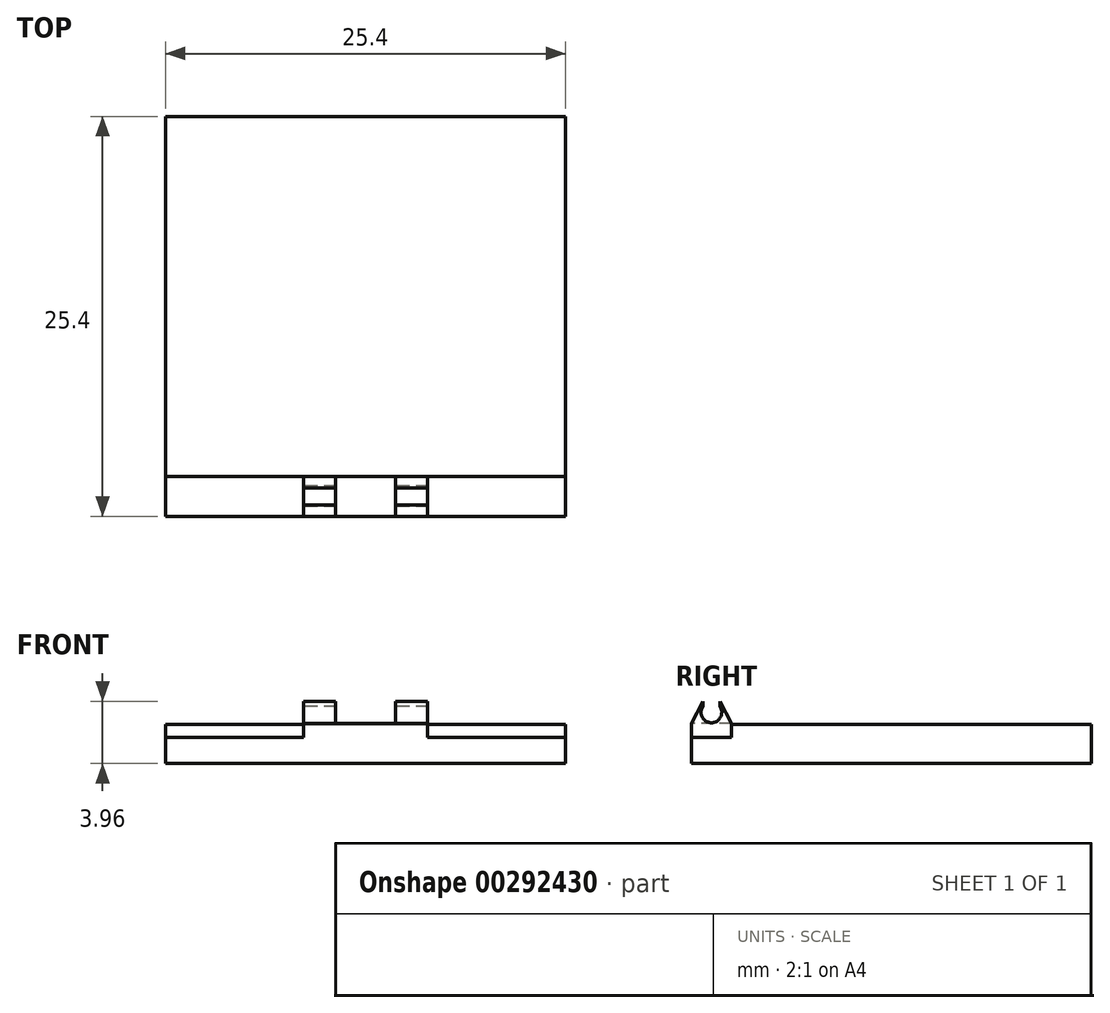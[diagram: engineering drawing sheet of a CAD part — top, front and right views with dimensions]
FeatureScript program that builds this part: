
annotation { "Feature Type Name" : "Feature", "Feature Type Description" : "" }
export const myFeature = defineFeature(function(context is Context, id is Id, definition is map)
    precondition{}
    {
        {
            var Q0;
            Q0=qCreatedBy(makeId("Top.planeOp"),FACE);
            var sketch = newSketch(context, id + "F0", { "sketchPlane" : qUnion([Q0])});
            skLineSegment(sketch, "E0.bottom", {"start": v(-9.72, 18.37) * mm, "end": v(15.68, 18.37) * mm});
            skLineSegment(sketch, "E0.top", {"start": v(-9.72, -7.03) * mm, "end": v(15.68, -7.03) * mm});
            skLineSegment(sketch, "E0.left", {"start": v(-9.72, 18.37) * mm, "end": v(-9.72, -7.03) * mm});
            skLineSegment(sketch, "E0.right", {"start": v(15.68, 18.37) * mm, "end": v(15.68, -7.03) * mm});
            skSolve(sketch);
        }
        {
            var Q0;
            Q0=qSketchRegion(id+"F0",true);
            extrude(context, id + "F1", {"entities" : qUnion([Q0]), "oppositeDirection" : true, "depth" : 2.54 * mm});
        }
        {
            var Q0;
            Q0=makeQuery(id+"F1.opExtrude","CAP_FACE",FACE,{"disambiguationData":[OSD([sQuery(id+"F0.wireOp",EDGE,"E0.bottom"),sQuery(id+"F0.wireOp",EDGE,"E0.top"),sQuery(id+"F0.wireOp",EDGE,"E0.left"),sQuery(id+"F0.wireOp",EDGE,"E0.right")])],"isStart":true});
            var sketch = newSketch(context, id + "F2", { "sketchPlane" : qUnion([Q0])});
            skLineSegment(sketch, "E1.bottom", {"start": v(-2.1, -7.03) * mm, "end": v(8.06, -7.03) * mm});
            skLineSegment(sketch, "E1.top", {"start": v(-2.1, -4.5) * mm, "end": v(8.06, -4.5) * mm});
            skLineSegment(sketch, "E1.left", {"start": v(-2.1, -7.03) * mm, "end": v(-2.1, -4.5) * mm});
            skLineSegment(sketch, "E1.right", {"start": v(8.06, -7.03) * mm, "end": v(8.06, -4.5) * mm});
            skSolve(sketch);
        }
        {
            var Q0;
            Q0=qSketchRegion(id+"F2",true);
            extrude(context, id + "F3", {"entities" : qUnion([Q0]), "operationType" : NewBodyOperationType.ADD, "depth" : 1.42 * mm});
        }
        {
            var Q0;
            Q0=makeQuery(id+"F3.opExtrude","SWEPT_FACE",FACE,{"disambiguationData":[OSD([sQuery(id+"F2.wireOp",EDGE,"E1.left")])]});
            var sketch = newSketch(context, id + "F4", { "sketchPlane" : qUnion([Q0])});
            skCircle(sketch, "E2", {"center": v(5.76, 0.71) * mm, "radius": 0.66 * mm});
            skPoint(sketch, "E3.endSnap0", {"position": v(5.76, 1.42) * mm});
            skLineSegment(sketch, "E4.bottom", {"start": v(5.22, 1.42) * mm, "end": v(6.32, 1.42) * mm});
            skLineSegment(sketch, "E4.left", {"start": v(5.22, 1.42) * mm, "end": v(5.22, 1.08) * mm});
            skLineSegment(sketch, "E4.right", {"start": v(6.32, 1.42) * mm, "end": v(6.32, 1.08) * mm});
            skLineSegment(sketch, "E5", {"start": v(5.22, 1.42) * mm, "end": v(4.5, 0) * mm});
            skLineSegment(sketch, "E6", {"start": v(6.32, 1.42) * mm, "end": v(7.03, 0) * mm});
            skSolve(sketch);
        }
        {
            var Q0;
            Q0=makeQuery(id+"F3.boolean.opBoolean","MERGE",FACE,{"derivedFrom":[makeQuery(id+"F1.opExtrude","SWEPT_FACE",FACE,{"disambiguationData":[OSD([sQuery(id+"F0.wireOp",EDGE,"E0.top")])]}),makeQuery(id+"F3.opExtrude","SWEPT_FACE",FACE,{"disambiguationData":[OSD([sQuery(id+"F2.wireOp",EDGE,"E1.bottom")])]})]});
            var sketch = newSketch(context, id + "F5", { "sketchPlane" : qUnion([Q0])});
            skLineSegment(sketch, "E7.bottom", {"start": v(-0.95, 1.42) * mm, "end": v(1.08, 1.42) * mm});
            skLineSegment(sketch, "E7.top", {"start": v(-0.95, 0) * mm, "end": v(1.08, 0) * mm});
            skLineSegment(sketch, "E7.left", {"start": v(-0.95, 1.42) * mm, "end": v(-0.95, 0) * mm});
            skLineSegment(sketch, "E7.right", {"start": v(1.08, 1.42) * mm, "end": v(1.08, 0) * mm});
            skLineSegment(sketch, "E8.bottom", {"start": v(4.89, 1.42) * mm, "end": v(6.92, 1.42) * mm});
            skLineSegment(sketch, "E8.top", {"start": v(4.89, 0) * mm, "end": v(6.92, 0) * mm});
            skLineSegment(sketch, "E8.left", {"start": v(4.89, 1.42) * mm, "end": v(4.89, 0) * mm});
            skLineSegment(sketch, "E8.right", {"start": v(6.92, 1.42) * mm, "end": v(6.92, 0) * mm});
            skLineSegment(sketch, "E9", {"start": v(-2.1, 0) * mm, "end": v(8.06, 0) * mm});
            skSolve(sketch);
        }
        {
            var Q0;
            {var subQ0=sQuery(id+"F5.wireOp",EDGE,"E7.left");Q0=makeQuery(id+"F5.imprint","IMPRINT",FACE,{"disambiguationData":[TD([[makeQuery(id+"F5.imprint","IMPRINT",EDGE,{"derivedFrom":subQ0}),-1.0]])]});}
            var Q1;
            {var subQ0=sQuery(id+"F5.wireOp",EDGE,"E7.right");Q1=makeQuery(id+"F5.imprint","IMPRINT",FACE,{"disambiguationData":[TD([[makeQuery(id+"F5.imprint","IMPRINT",EDGE,{"derivedFrom":subQ0}),1.0]])]});}
            var Q2;
            {var subQ0=sQuery(id+"F5.wireOp",EDGE,"E8.right");Q2=makeQuery(id+"F5.imprint","IMPRINT",FACE,{"disambiguationData":[TD([[makeQuery(id+"F5.imprint","IMPRINT",EDGE,{"derivedFrom":subQ0}),1.0]])]});}
            extrude(context, id + "F6", {"entities" : qUnion([Q0, Q1, Q2]), "operationType" : NewBodyOperationType.REMOVE, "oppositeDirection" : true, "depth" : 25.4 * mm});
        }
        {
            var Q0;
            {var subQ0=sQuery(id+"F4.wireOp",EDGE,"E5");Q0=makeQuery(id+"F4.imprint","IMPRINT",FACE,{"disambiguationData":[TD([[makeQuery(id+"F4.imprint","IMPRINT",EDGE,{"derivedFrom":subQ0}),-1.0]])]});}
            var Q1;
            {var subQ0=sQuery(id+"F4.wireOp",EDGE,"E2");var subQ1=makeQuery(id+"F4.imprint","INTERSECT",VERTEX,{"derivedFrom":[subQ0,sQuery(id+"F4.wireOp",EDGE,"E4.right")]});Q1=makeQuery(id+"F4.imprint","IMPRINT",FACE,{"disambiguationData":[TD([[makeQuery(id+"F4.imprint","IMPRINT",EDGE,{"disambiguationData":[TD([[subQ1,-1.0]])],"derivedFrom":subQ0}),1.0]])]});}
            var Q2;
            {var subQ4=sQuery(id+"F4.wireOp",EDGE,"E4.bottom");Q2=makeQuery(id+"F4.imprint","IMPRINT",FACE,{"disambiguationData":[TD([[makeQuery(id+"F4.imprint","IMPRINT",EDGE,{"derivedFrom":subQ4}),1.0]])]});}
            var Q3;
            {var subQ0=sQuery(id+"F4.wireOp",EDGE,"E6");Q3=makeQuery(id+"F4.imprint","IMPRINT",FACE,{"disambiguationData":[TD([[makeQuery(id+"F4.imprint","IMPRINT",EDGE,{"derivedFrom":subQ0}),1.0]])]});}
            extrude(context, id + "F7", {"entities" : qUnion([Q0, Q1, Q2, Q3]), "operationType" : NewBodyOperationType.REMOVE, "oppositeDirection" : true, "depth" : 25.4 * mm});
        }
        {
            var Q0;
            {var subQ0=sQuery(id+"F5.wireOp",EDGE,"E9");var subQ1=sQuery(id+"F0.wireOp",EDGE,"E0.right");var subQ4=sQuery(id+"F0.wireOp",EDGE,"E0.left");var subQ5=sQuery(id+"F0.wireOp",EDGE,"E0.top");var subQ6=makeQuery(id+"F1.opExtrude","CAP_FACE",FACE,{"disambiguationData":[OSD([sQuery(id+"F0.wireOp",EDGE,"E0.bottom"),subQ5,subQ4,subQ1])],"isStart":true});Q0=makeQuery(id+"F6.boolean.opBoolean","MERGE",FACE,{"derivedFrom":[subQ6,makeQuery(id+"F6.opExtrude","SWEPT_FACE",FACE,{"disambiguationData":[OSD([subQ0]),TDD([makeQuery(id+"F5.imprint","IMPRINT",EDGE,{"disambiguationData":[TD([[makeQuery(id+"F5.imprint","INTERSECT",VERTEX,{"derivedFrom":[sQuery(id+"F5.wireOp",EDGE,"E7.left"),subQ0]}),1.0]])],"derivedFrom":subQ0})])]}),makeQuery(id+"F6.opExtrude","SWEPT_FACE",FACE,{"disambiguationData":[OSD([subQ0]),TDD([makeQuery(id+"F5.imprint","IMPRINT",EDGE,{"disambiguationData":[TD([[makeQuery(id+"F5.imprint","INTERSECT",VERTEX,{"derivedFrom":[sQuery(id+"F5.wireOp",EDGE,"E7.right"),subQ0]}),-1.0]])],"derivedFrom":subQ0})])]}),makeQuery(id+"F6.opExtrude","SWEPT_FACE",FACE,{"disambiguationData":[OSD([subQ0]),TDD([makeQuery(id+"F5.imprint","IMPRINT",EDGE,{"disambiguationData":[TD([[makeQuery(id+"F5.imprint","INTERSECT",VERTEX,{"derivedFrom":[sQuery(id+"F5.wireOp",EDGE,"E8.right"),subQ0]}),-1.0]])],"derivedFrom":subQ0})])]})]});}
            var sketch = newSketch(context, id + "F8", { "sketchPlane" : qUnion([Q0])});
            skLineSegment(sketch, "E10.bottom", {"start": v(6.92, -4.5) * mm, "end": v(15.68, -4.5) * mm});
            skLineSegment(sketch, "E10.top", {"start": v(6.92, -7.03) * mm, "end": v(15.68, -7.03) * mm});
            skLineSegment(sketch, "E10.left", {"start": v(6.92, -4.5) * mm, "end": v(6.92, -7.03) * mm});
            skLineSegment(sketch, "E10.right", {"start": v(15.68, -4.5) * mm, "end": v(15.68, -7.03) * mm});
            skLineSegment(sketch, "E11.bottom", {"start": v(-0.95, -4.5) * mm, "end": v(-9.72, -4.5) * mm});
            skLineSegment(sketch, "E11.top", {"start": v(-0.95, -7.03) * mm, "end": v(-9.72, -7.03) * mm});
            skLineSegment(sketch, "E11.left", {"start": v(-0.95, -4.5) * mm, "end": v(-0.95, -7.03) * mm});
            skLineSegment(sketch, "E11.right", {"start": v(-9.72, -4.5) * mm, "end": v(-9.72, -7.03) * mm});
            skSolve(sketch);
        }
        {
            var Q0;
            Q0=qSketchRegion(id+"F8",true);
            extrude(context, id + "F9", {"entities" : qUnion([Q0]), "operationType" : NewBodyOperationType.REMOVE, "oppositeDirection" : true, "depth" : 0.89 * mm});
        }
        {
            var Q0;
            Q0=makeQuery(id+"F1.opExtrude","SWEPT_FACE",FACE,{"disambiguationData":[OSD([sQuery(id+"F0.wireOp",EDGE,"E0.right")])]});
            var sketch = newSketch(context, id + "F10", { "sketchPlane" : qUnion([Q0])});
            skLineSegment(sketch, "E12", {"start": v(-4.5, -0.05) * mm, "end": v(18.37, -0.05) * mm});
            skLineSegment(sketch, "E13", {"start": v(18.37, -0.05) * mm, "end": v(18.37, 0) * mm});
            skLineSegment(sketch, "E14", {"start": v(18.37, 0) * mm, "end": v(-4.5, 0) * mm});
            skLineSegment(sketch, "E15", {"start": v(-4.5, 0) * mm, "end": v(-4.5, -0.05) * mm});
            skSolve(sketch);
        }
        {
            var Q0;
            Q0=qSketchRegion(id+"F10",true);
            extrude(context, id + "F11", {"entities" : qUnion([Q0]), "operationType" : NewBodyOperationType.REMOVE, "oppositeDirection" : true, "depth" : 25.4 * mm});
        }
    });
